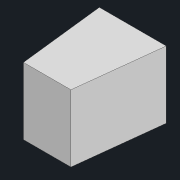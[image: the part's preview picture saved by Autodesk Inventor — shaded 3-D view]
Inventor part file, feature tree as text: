
AUTODESK INVENTOR PART (.ipt)
format: ipt  version: 2022.3 (Build 263350000, 350)  size: 82,432 bytes
history: native  units: in
note: dims shown in document units (in); Inventor stores cm internally (conversion verified against a paired STEP export)
features: extrude x1, sketch x1
ambient origin geometry x8: Origin, YZ Plane, XZ Plane, XY Plane, X Axis, Y Axis, Z Axis, Center Point
bodies: Body1 (feature_tree)
feature tree (2):
  extrude  "Extrusion1"  Depth=1.0in
  sketch  "Sketch1"  dims[d6=0.7087in d27=1.0in d28=1.0in d29=0.0in]
